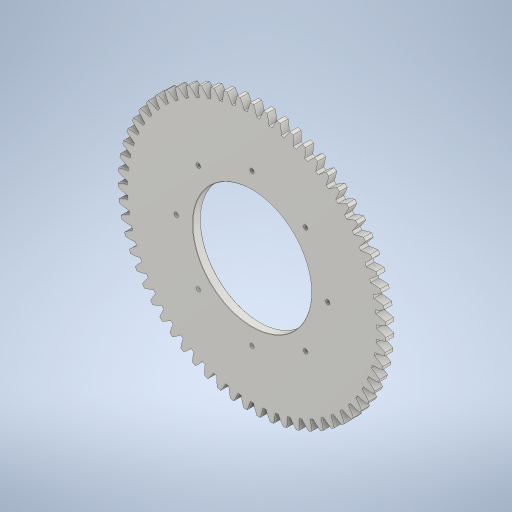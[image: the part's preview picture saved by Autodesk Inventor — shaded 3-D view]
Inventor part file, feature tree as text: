
AUTODESK INVENTOR PART (.ipt)
format: ipt  version: 2024.2 (Build 282272000, 272)  size: 706,560 bytes
history: native  units: mm (DEFAULTED — no unit token found)
features: extrude x3, plane x3, other x3, sketch x3, pattern_circular x1, fillet x1, projected_geometry x1
ambient origin geometry x8: Origin, YZ Plane, XZ Plane, XY Plane, X Axis, Y Axis, Z Axis, Center Point
bodies: Solid1 (feature_tree)
feature tree (15):
  extrude  "Extrusion1"  Depth=24.0mm TaperAngle=0.0deg
  plane  "Work Plane2"
  plane  "Work Plane8"
  plane  "Work Plane9"
  other  "Spur Gear"
  extrude  "Extrusion2"  Depth=10.0mm TaperAngle=0.0deg
  extrude  "Extrusion3"  Depth=1.0mm TaperAngle=0.0deg
  pattern_circular  "Circular Pattern1"  [2 undecoded]
  fillet  "Fillet1"  [1 undecoded]
  sketch  "Sketch1"  dims[d0=812.91152mm d1=24.0mm d2=0.0mm]
  other  "Srf1"
  sketch  "Sketch3"  dims[d3=787.89816mm d4=10.0mm d5=0.0mm]
  projected_geometry  "Projected Loop1"
  sketch  "Sketch4"  dims[d16=494.0mm d17=0.0mm d34=0.498666mm d39=0.0mm d41=0.0mm d43=494.0mm d46=494.0mm d47=0.0mm d48=0.0mm d49=360.0mm d50=0.0mm d51=0.0mm d52=12.5mm d53=230.0mm d54=0.0mm d55=0.0mm d56=80.0mm d57=360.0deg d59=1.0mm]
  other  "Pitch Diameter"
note: 3 required parameter values undecoded (feature->parameter linkage not recoverable at this tier; creation-order binding heuristic only, values carry confidence <= 0.55)
